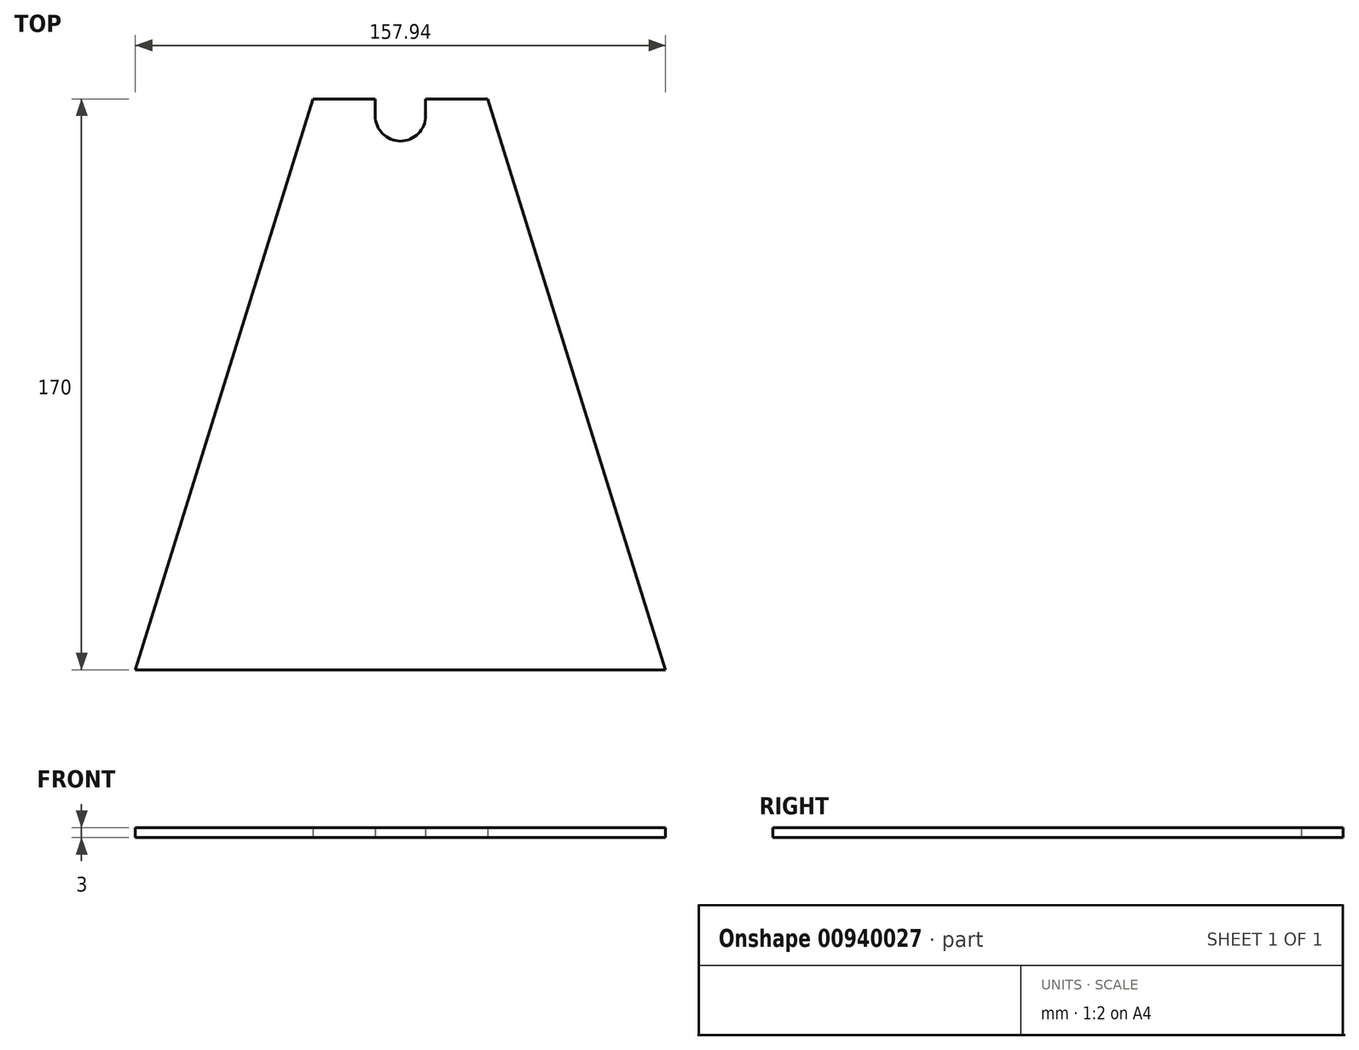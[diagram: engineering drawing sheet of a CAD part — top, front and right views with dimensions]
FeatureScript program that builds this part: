
annotation { "Feature Type Name" : "Feature", "Feature Type Description" : "" }
export const myFeature = defineFeature(function(context is Context, id is Id, definition is map)
    precondition{}
    {
        {
            var Q0;
            Q0=qCreatedBy(makeId("Top.planeOp"),FACE);
            var sketch = newSketch(context, id + "F0", { "sketchPlane" : qUnion([Q0])});
            skLineSegment(sketch, "E0", {"start": v(0, 0) * mm, "end": v(78.97, 0) * mm});
            skLineSegment(sketch, "E1", {"start": v(78.97, 0) * mm, "end": v(26.02, 170) * mm});
            skLineSegment(sketch, "E2", {"start": v(26.02, 170) * mm, "end": v(7.5, 170) * mm});
            skLineSegment(sketch, "E3", {"start": v(7.5, 170) * mm, "end": v(7.5, 165) * mm});
            skArc(sketch, "E4", {"start": v(0, 157.5) * mm, "mid": v(5.3, 159.7) * mm, "end": v(7.5, 165) * mm});
            skLineSegment(sketch, "E5", {"start": v(0, 0) * mm, "end": v(0, 237.57) * mm, "construction": true});
            skPoint(sketch, "E6.orphan", {"position": v(-7.5, 165) * mm});
            skArc(sketch, "E7.MirrorCS", {"start": v(0, 157.5) * mm, "mid": v(-5.3, 159.7) * mm, "end": v(-7.5, 165) * mm});
            skLineSegment(sketch, "E8.MirrorCS", {"start": v(-7.5, 170) * mm, "end": v(-7.5, 165) * mm});
            skLineSegment(sketch, "E9.MirrorCS", {"start": v(-26.02, 170) * mm, "end": v(-7.5, 170) * mm});
            skLineSegment(sketch, "E10.MirrorCS", {"start": v(-78.97, 0) * mm, "end": v(-26.02, 170) * mm});
            skLineSegment(sketch, "E11.MirrorCS", {"start": v(0, 0) * mm, "end": v(-78.97, 0) * mm});
            skSolve(sketch);
        }
        {
            var Q0;
            Q0 = qSketchRegion(id + "F0", true);
            extrude(context, id + "F1", {"entities" : qUnion([Q0]), "depth" : 3 * mm, "offsetDistance" : 25 * mm});
        }
    });
